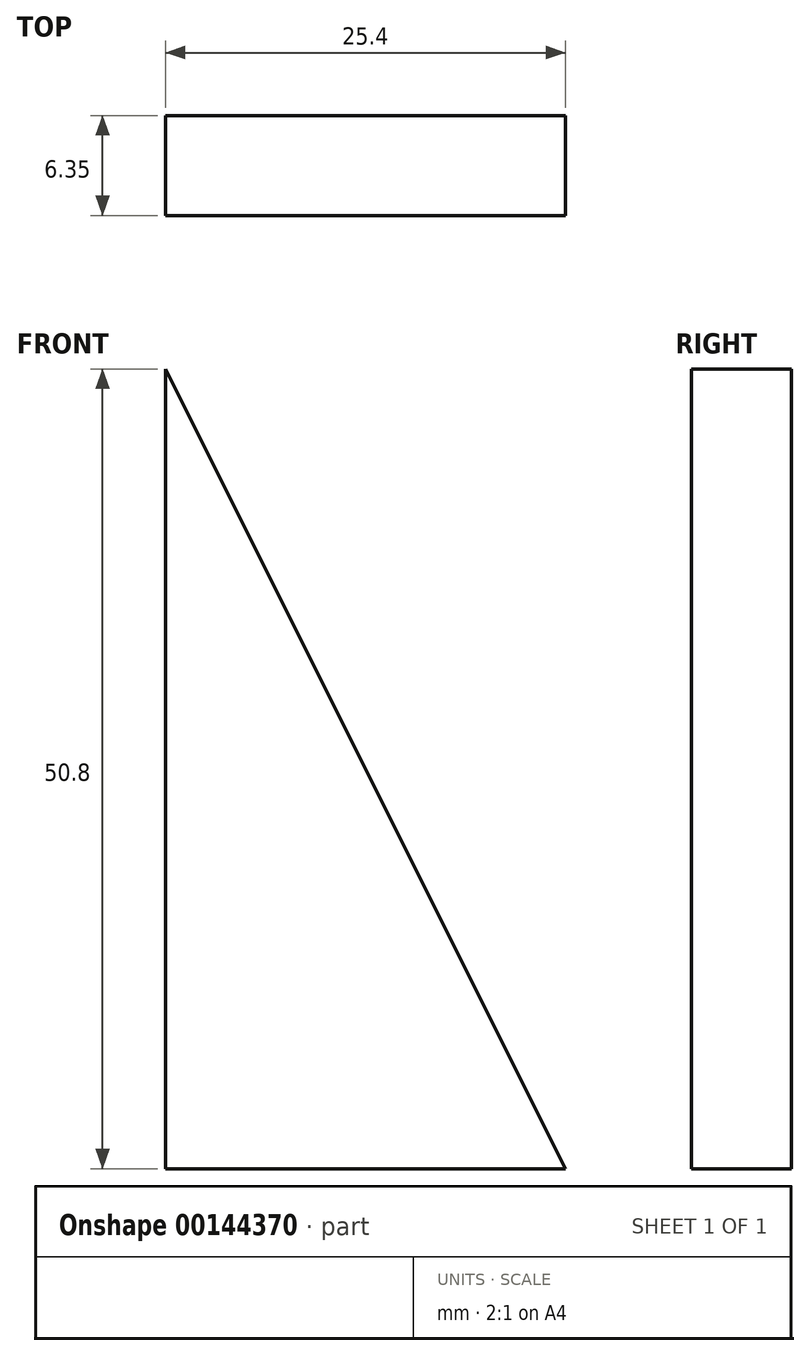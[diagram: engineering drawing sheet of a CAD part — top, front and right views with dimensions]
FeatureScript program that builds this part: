
annotation { "Feature Type Name" : "Feature", "Feature Type Description" : "" }
export const myFeature = defineFeature(function(context is Context, id is Id, definition is map)
    precondition{}
    {
        {
            var Q0;
            Q0=qCreatedBy(makeId("Front.planeOp"),FACE);
            var sketch = newSketch(context, id + "F0", { "sketchPlane" : qUnion([Q0])});
            skLineSegment(sketch, "E0", {"start": v(0, 0) * mm, "end": v(0, 50.8) * mm});
            skLineSegment(sketch, "E1", {"start": v(0, 50.8) * mm, "end": v(25.4, 0) * mm});
            skLineSegment(sketch, "E2", {"start": v(25.4, 0) * mm, "end": v(0, 0) * mm});
            skSolve(sketch);
        }
        {
            var Q0;
            Q0 = qSketchRegion(id + "F0", true);
            extrude(context, id + "F1", {"entities" : qUnion([Q0]), "depth" : 6.35 * mm});
        }
    });
